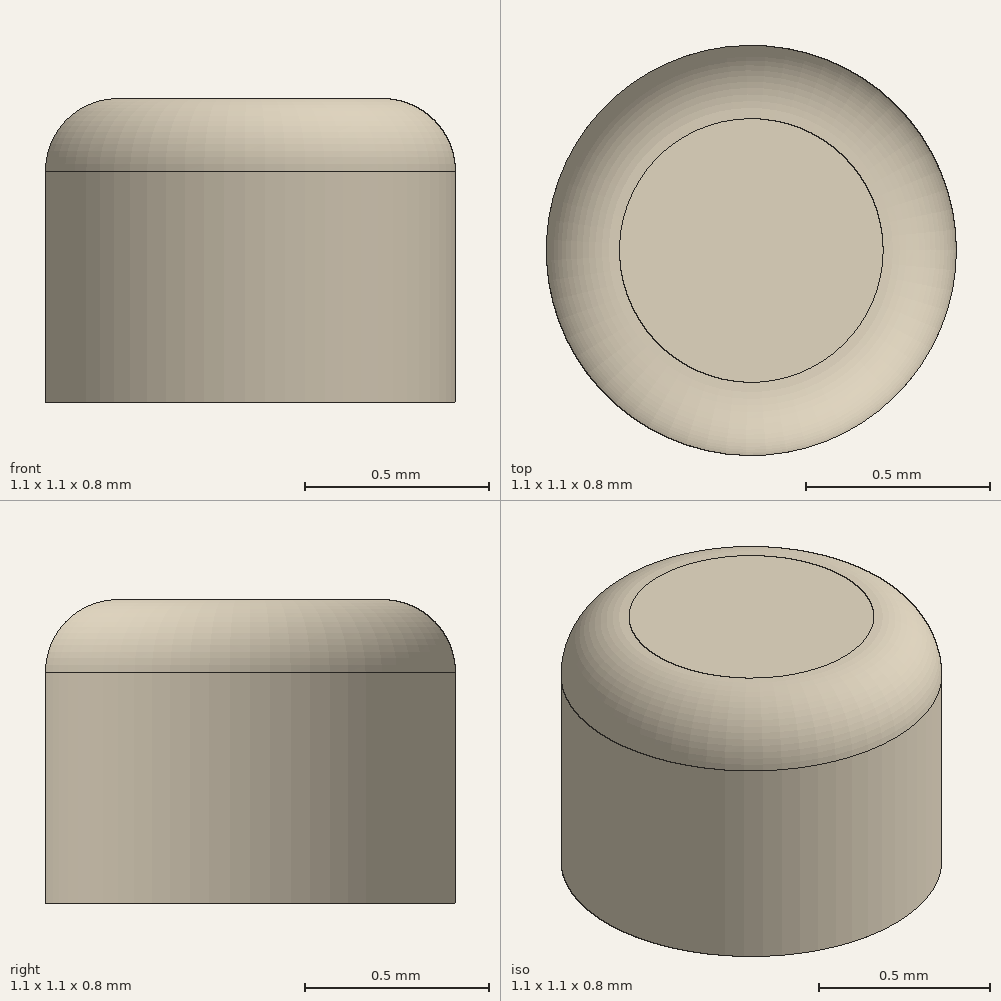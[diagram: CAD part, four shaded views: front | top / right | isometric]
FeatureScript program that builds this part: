
annotation { "Feature Type Name" : "Feature", "Feature Type Description" : "" }
export const myFeature = defineFeature(function(context is Context, id is Id, definition is map)
    precondition{}
    {
        {
            var Q0;
            Q0=qCreatedBy(makeId("Top.planeOp"),FACE);
            var sketch = newSketch(context, id + "F0", { "sketchPlane" : qUnion([Q0])});
            skCircle(sketch, "E0", {"center": v(0, 0) * mm, "radius": 0.56 * mm});
            skSolve(sketch);
        }
        {
            var Q0;
            Q0 = qSketchRegion(id + "F0", true);
            extrude(context, id + "F1", {"entities" : qUnion([Q0]), "depth" : .83 * mm});
        }
        {
            var Q0;
            Q0=makeQuery(id+"F1.opExtrude","CAP_FACE",FACE,{"disambiguationData":[OSD([sQuery(id+"F0.wireOp",EDGE,"E0")])],"isStart":true});
            var sketch = newSketch(context, id + "F2", { "sketchPlane" : qUnion([Q0])});
            skCircle(sketch, "E1", {"center": v(0, 0) * mm, "radius": 0.34 * mm});
            skSolve(sketch);
        }
        {
            var Q0;
            Q0=makeQuery(id+"F2.imprint","IMPRINT",FACE,{"disambiguationData":[TD([[makeQuery(id+"F2.imprint","IMPRINT",EDGE,{"derivedFrom":sQuery(id+"F2.wireOp",EDGE,"E1")}),1.0]])]});
            extrude(context, id + "F3", {"entities" : qUnion([Q0]), "operationType" : NewBodyOperationType.REMOVE, "oppositeDirection" : true, "depth" : .4 * mm});
        }
        {
            var Q0;
            Q0=makeQuery(id+"F1.opExtrude","CAP_EDGE",EDGE,{"disambiguationData":[OSD([sQuery(id+"F0.wireOp",EDGE,"E0")])],"isStart":false});
            fillet(context, id + "F4", {"entities" : qUnion([Q0]), "radius" : .2 * mm, "tangentPropagation" : true, "allowEdgeOverflow" : false});
        }
    });
